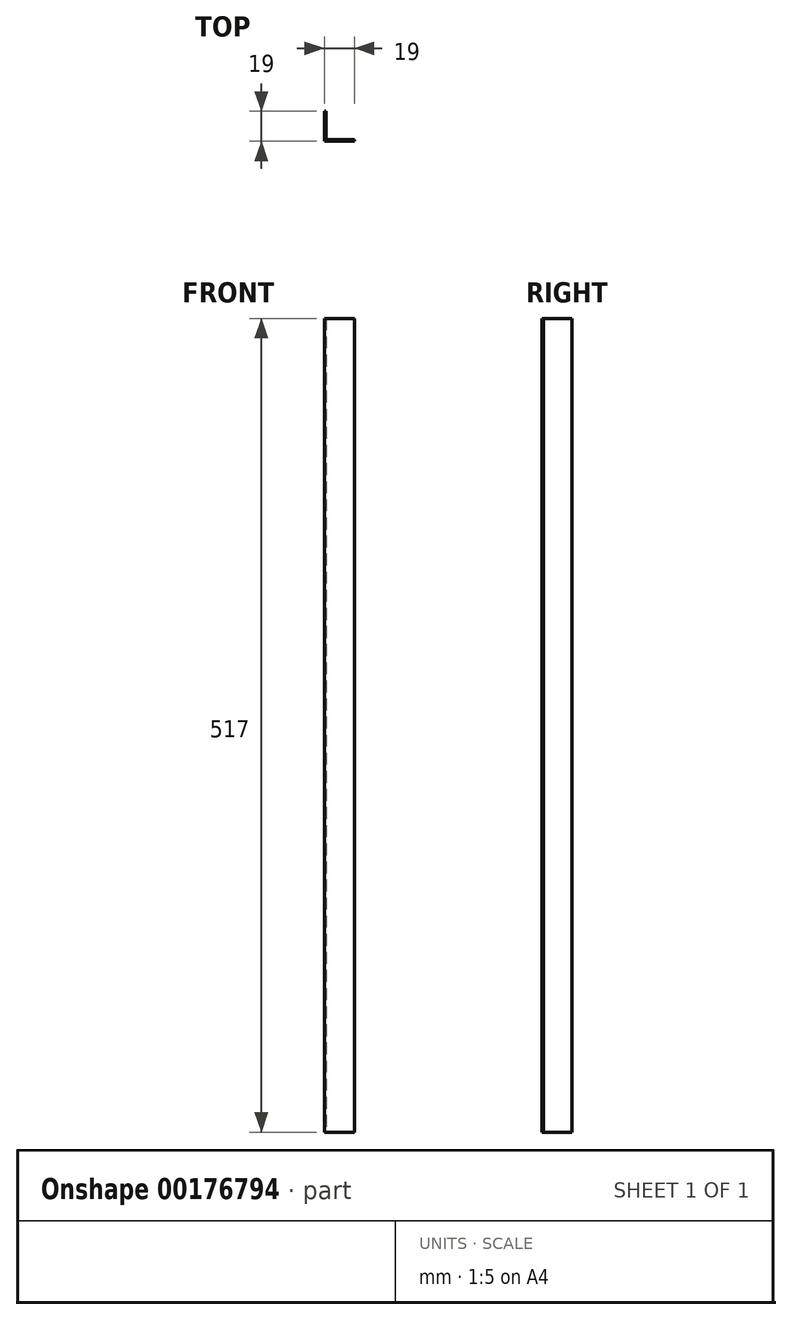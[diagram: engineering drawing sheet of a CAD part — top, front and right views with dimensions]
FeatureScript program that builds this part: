
annotation { "Feature Type Name" : "Feature", "Feature Type Description" : "" }
export const myFeature = defineFeature(function(context is Context, id is Id, definition is map)
    precondition{}
    {
        {
            var Q0;
            Q0=qCreatedBy(makeId("Top.planeOp"),FACE);
            var sketch = newSketch(context, id + "F0", { "sketchPlane" : qUnion([Q0])});
            skLineSegment(sketch, "E0", {"start": v(-4.33, -9.84) * mm, "end": v(14.67, -9.84) * mm});
            skLineSegment(sketch, "E1", {"start": v(-4.33, -9.84) * mm, "end": v(-4.33, 9.16) * mm});
            skLineSegment(sketch, "E2", {"start": v(-4.33, 9.16) * mm, "end": v(-3.33, 9.16) * mm});
            skLineSegment(sketch, "E3", {"start": v(-3.33, 9.16) * mm, "end": v(-3.33, -8.84) * mm});
            skLineSegment(sketch, "E4", {"start": v(-3.33, -8.84) * mm, "end": v(14.67, -8.84) * mm});
            skLineSegment(sketch, "E5", {"start": v(14.67, -8.84) * mm, "end": v(14.67, -9.84) * mm});
            skSolve(sketch);
        }
        {
            var Q0;
            Q0=makeQuery(id+"F0.imprint","IMPRINT",FACE,{"disambiguationData":[TD([[makeQuery(id+"F0.imprint","IMPRINT",EDGE,{"derivedFrom":sQuery(id+"F0.wireOp",EDGE,"E0")}),1.0]])]});
            extrude(context, id + "F1", {"entities" : qUnion([Q0]), "depth" : 517 * mm});
        }
    });
